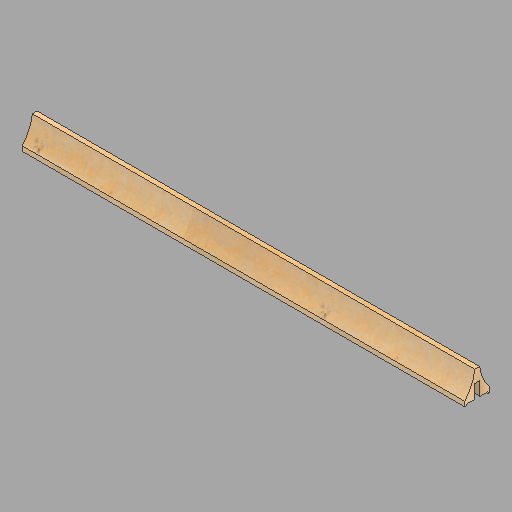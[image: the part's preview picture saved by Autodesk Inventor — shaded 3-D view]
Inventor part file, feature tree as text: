
AUTODESK INVENTOR PART (.ipt)
format: ipt  version: 2022.2 (Build 262287010, 287A)  size: 178,176 bytes
history: native  units: in
note: dims shown in document units (in); Inventor stores cm internally (conversion verified against a paired STEP export)
features: revolve x2, direct_edit x1, other x1
ambient origin geometry x8: Origin, YZ Plane, XZ Plane, XY Plane, X Axis, Y Axis, Z Axis, Center Point
bodies: Solid1 (feature_tree)
feature tree (4):
  direct_edit  "Direct Edit1"
  other  "Mull (lower)"
  revolve  "Rotate1"  [1 undecoded]
  revolve  "Rotate2"  Angle=180.0deg
note: 1 required parameter value undecoded (feature->parameter linkage not recoverable at this tier; creation-order binding heuristic only, values carry confidence <= 0.55)
